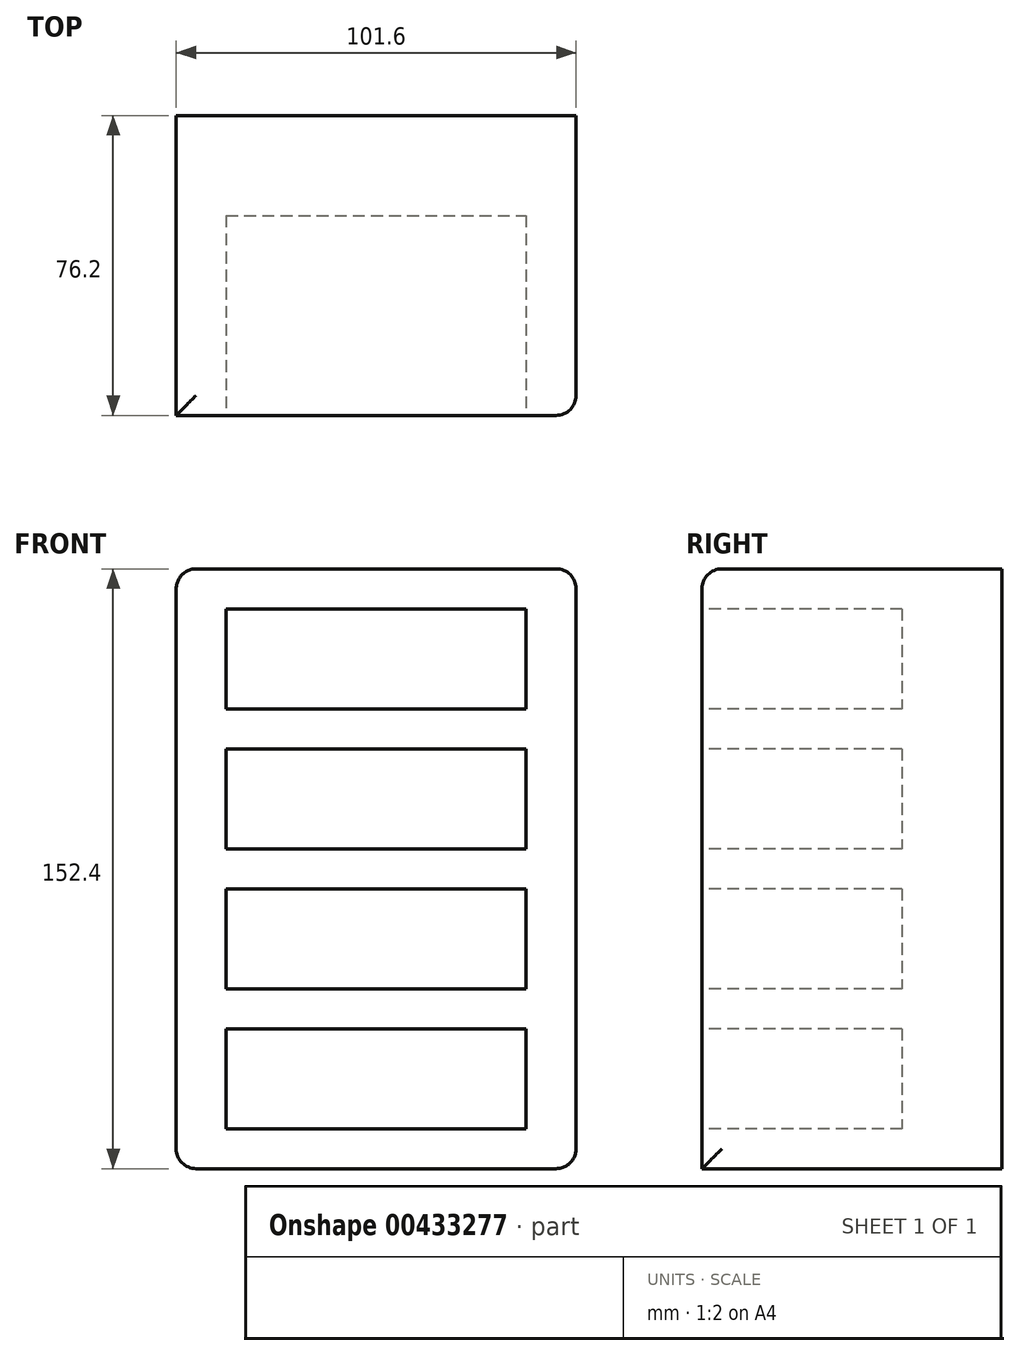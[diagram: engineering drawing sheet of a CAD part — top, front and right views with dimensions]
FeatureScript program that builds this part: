
annotation { "Feature Type Name" : "Feature", "Feature Type Description" : "" }
export const myFeature = defineFeature(function(context is Context, id is Id, definition is map)
    precondition{}
    {
        {
            var Q0;
            Q0=qCreatedBy(makeId("Front.planeOp"),FACE);
            var sketch = newSketch(context, id + "F0", { "sketchPlane" : qUnion([Q0])});
            skLineSegment(sketch, "E0.bottom", {"start": v(-16.05, 58.71) * mm, "end": v(85.55, 58.71) * mm});
            skLineSegment(sketch, "E0.top", {"start": v(-16.05, -93.69) * mm, "end": v(85.55, -93.69) * mm});
            skLineSegment(sketch, "E0.left", {"start": v(-16.05, 58.71) * mm, "end": v(-16.05, -93.69) * mm});
            skLineSegment(sketch, "E0.right", {"start": v(85.55, 58.71) * mm, "end": v(85.55, -93.69) * mm});
            skSolve(sketch);
        }
        {
            var Q0;
            Q0=makeQuery(id+"F0.imprint","IMPRINT",FACE,{"disambiguationData":[TD([[makeQuery(id+"F0.imprint","IMPRINT",EDGE,{"derivedFrom":sQuery(id+"F0.wireOp",EDGE,"E0.bottom")}),-1.0]])]});
            extrude(context, id + "F1", {"entities" : qUnion([Q0]), "depth" : 76.2 * mm});
        }
        {
            var Q0;
            Q0=makeQuery(id+"F1.opExtrude","CAP_FACE",FACE,{"disambiguationData":[OSD([sQuery(id+"F0.wireOp",EDGE,"E0.bottom"),sQuery(id+"F0.wireOp",EDGE,"E0.top"),sQuery(id+"F0.wireOp",EDGE,"E0.left"),sQuery(id+"F0.wireOp",EDGE,"E0.right")])],"isStart":false});
            var sketch = newSketch(context, id + "F2", { "sketchPlane" : qUnion([Q0])});
            skLineSegment(sketch, "E1.bottom", {"start": v(-3.35, 48.55) * mm, "end": v(72.85, 48.55) * mm});
            skLineSegment(sketch, "E1.top", {"start": v(-3.35, 23.15) * mm, "end": v(72.85, 23.15) * mm});
            skLineSegment(sketch, "E1.left", {"start": v(-3.35, 48.55) * mm, "end": v(-3.35, 23.15) * mm});
            skLineSegment(sketch, "E1.right", {"start": v(72.85, 48.55) * mm, "end": v(72.85, 23.15) * mm});
            skLineSegment(sketch, "E2.0.1.0", {"start": v(-3.35, 13) * mm, "end": v(-3.35, -12.4) * mm});
            skLineSegment(sketch, "E2.0.1.1", {"start": v(-3.35, 13) * mm, "end": v(72.85, 13) * mm});
            skLineSegment(sketch, "E2.0.1.2", {"start": v(72.85, 13) * mm, "end": v(72.85, -12.4) * mm});
            skLineSegment(sketch, "E2.0.1.3", {"start": v(-3.35, -12.4) * mm, "end": v(72.85, -12.4) * mm});
            skLineSegment(sketch, "E2.0.2.0", {"start": v(-3.35, -22.57) * mm, "end": v(-3.35, -47.97) * mm});
            skLineSegment(sketch, "E2.0.2.1", {"start": v(-3.35, -22.57) * mm, "end": v(72.85, -22.57) * mm});
            skLineSegment(sketch, "E2.0.2.2", {"start": v(72.85, -22.57) * mm, "end": v(72.85, -47.97) * mm});
            skLineSegment(sketch, "E2.0.2.3", {"start": v(-3.35, -47.97) * mm, "end": v(72.85, -47.97) * mm});
            skLineSegment(sketch, "E2.0.3.0", {"start": v(-3.35, -58.13) * mm, "end": v(-3.35, -83.53) * mm});
            skLineSegment(sketch, "E2.0.3.1", {"start": v(-3.35, -58.13) * mm, "end": v(72.85, -58.13) * mm});
            skLineSegment(sketch, "E2.0.3.2", {"start": v(72.85, -58.13) * mm, "end": v(72.85, -83.53) * mm});
            skLineSegment(sketch, "E2.0.3.3", {"start": v(-3.35, -83.53) * mm, "end": v(72.85, -83.53) * mm});
            skLineSegment(sketch, "E2.direction1", {"start": v(-3.35, 23.15) * mm, "end": v(22.05, 23.15) * mm, "construction": true});
            skLineSegment(sketch, "E2.direction2", {"start": v(-3.35, 23.15) * mm, "end": v(-3.35, -12.4) * mm, "construction": true});
            skSolve(sketch);
        }
        {
            var Q0;
            Q0=makeQuery(id+"F2.imprint","IMPRINT",FACE,{"disambiguationData":[TD([[makeQuery(id+"F2.imprint","IMPRINT",EDGE,{"derivedFrom":sQuery(id+"F2.wireOp",EDGE,"E1.bottom")}),-1.0]])]});
            var Q1;
            Q1=makeQuery(id+"F2.imprint","IMPRINT",FACE,{"disambiguationData":[TD([[makeQuery(id+"F2.imprint","IMPRINT",EDGE,{"derivedFrom":sQuery(id+"F2.wireOp",EDGE,"E2.0.1.0")}),1.0]])]});
            var Q2;
            Q2=makeQuery(id+"F2.imprint","IMPRINT",FACE,{"disambiguationData":[TD([[makeQuery(id+"F2.imprint","IMPRINT",EDGE,{"derivedFrom":sQuery(id+"F2.wireOp",EDGE,"E2.0.2.0")}),1.0]])]});
            var Q3;
            Q3=makeQuery(id+"F2.imprint","IMPRINT",FACE,{"disambiguationData":[TD([[makeQuery(id+"F2.imprint","IMPRINT",EDGE,{"derivedFrom":sQuery(id+"F2.wireOp",EDGE,"E2.0.3.0")}),1.0]])]});
            extrude(context, id + "F3", {"entities" : qUnion([Q0, Q1, Q2, Q3]), "operationType" : NewBodyOperationType.REMOVE, "oppositeDirection" : true, "depth" : 50.8 * mm});
        }
        {
            var Q0;
            Q0=makeQuery(id+"F1.opExtrude","CAP_EDGE",EDGE,{"disambiguationData":[OSD([sQuery(id+"F0.wireOp",EDGE,"E0.bottom")])],"isStart":false});
            var Q1;
            Q1=makeQuery(id+"F1.opExtrude","SWEPT_EDGE",EDGE,{"disambiguationData":[OSD([sQuery(id+"F0.wireOp",EDGE,"E0.bottom"),sQuery(id+"F0.wireOp",EDGE,"E0.right")])]});
            var Q2;
            Q2=makeQuery(id+"F1.opExtrude","SWEPT_EDGE",EDGE,{"disambiguationData":[OSD([sQuery(id+"F0.wireOp",EDGE,"E0.top"),sQuery(id+"F0.wireOp",EDGE,"E0.right")])]});
            var Q3;
            Q3=makeQuery(id+"F1.opExtrude","SWEPT_EDGE",EDGE,{"disambiguationData":[OSD([sQuery(id+"F0.wireOp",EDGE,"E0.top"),sQuery(id+"F0.wireOp",EDGE,"E0.left")])]});
            var Q4;
            Q4=makeQuery(id+"F1.opExtrude","SWEPT_EDGE",EDGE,{"disambiguationData":[OSD([sQuery(id+"F0.wireOp",EDGE,"E0.bottom"),sQuery(id+"F0.wireOp",EDGE,"E0.left")])]});
            var Q5;
            Q5=makeQuery(id+"F1.opExtrude","CAP_EDGE",EDGE,{"disambiguationData":[OSD([sQuery(id+"F0.wireOp",EDGE,"E0.right")])],"isStart":false});
            fillet(context, id + "F4", {"entities" : qUnion([Q0, Q1, Q2, Q3, Q4, Q5]), "radius" : 5.08 * mm, "tangentPropagation" : true, "allowEdgeOverflow" : false});
        }
    });
